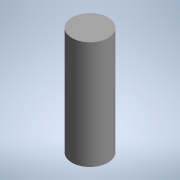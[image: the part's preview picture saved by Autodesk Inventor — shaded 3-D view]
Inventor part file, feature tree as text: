
AUTODESK INVENTOR PART (.ipt)
format: ipt  version: 2022 (Build 260153000, 153)  size: 71,168 bytes
history: native  units: mm (DEFAULTED — no unit token found)
features: extrude x1, sketch x1
ambient origin geometry x8: Origin, YZ Plane, XZ Plane, XY Plane, X Axis, Y Axis, Z Axis, Center Point
bodies: Solid1 (feature_tree)
feature tree (2):
  extrude  "Extrusion1"  Depth=30.0mm TaperAngle=0.0deg
  sketch  "Sketch1"  dims[d0=10.0mm d1=30.0mm d2=0.0mm]
